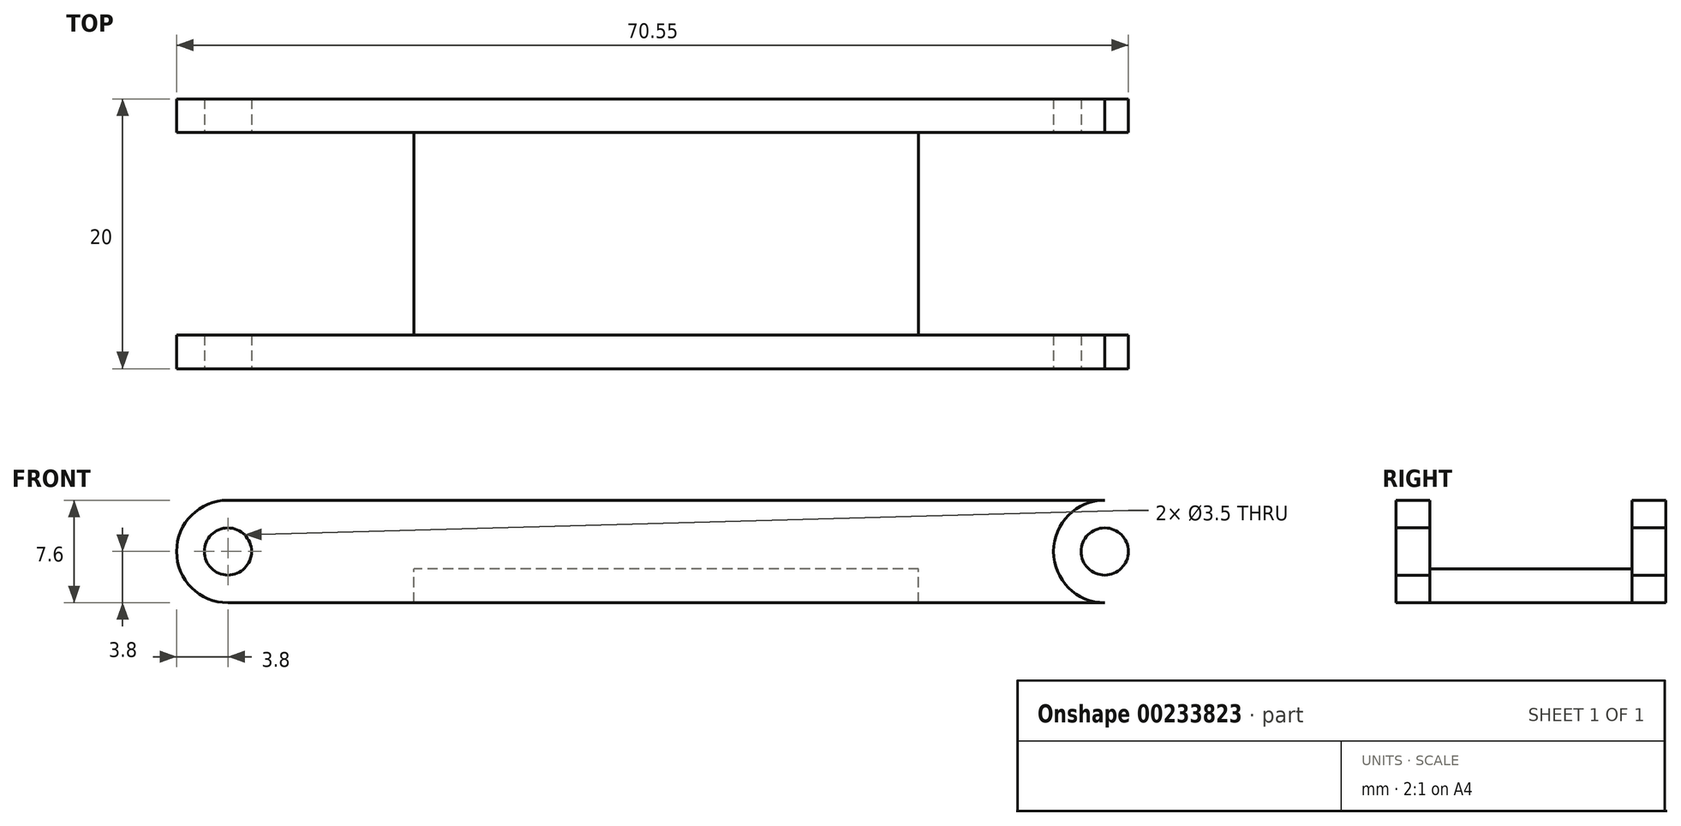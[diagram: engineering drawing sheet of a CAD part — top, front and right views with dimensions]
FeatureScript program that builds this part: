
annotation { "Feature Type Name" : "Feature", "Feature Type Description" : "" }
export const myFeature = defineFeature(function(context is Context, id is Id, definition is map)
    precondition{}
    {
        {
            var Q0;
            Q0=qCreatedBy(makeId("Right.planeOp"),FACE);
            var sketch = newSketch(context, id + "F0", { "sketchPlane" : qUnion([Q0])});
            skLineSegment(sketch, "E0.bottom", {"start": v(-7.5, 0) * mm, "end": v(7.5, 0) * mm});
            skLineSegment(sketch, "E0.top", {"start": v(-7.5, 2.5) * mm, "end": v(7.5, 2.5) * mm});
            skLineSegment(sketch, "E0.left", {"start": v(-7.5, 0) * mm, "end": v(-7.5, 2.5) * mm});
            skLineSegment(sketch, "E0.right", {"start": v(7.5, 0) * mm, "end": v(7.5, 2.5) * mm});
            skLineSegment(sketch, "E1.bottom", {"start": v(-7.5, 0) * mm, "end": v(-10, 0) * mm});
            skLineSegment(sketch, "E1.top", {"start": v(-7.5, 7.6) * mm, "end": v(-10, 7.6) * mm});
            skLineSegment(sketch, "E1.left", {"start": v(-7.5, 0) * mm, "end": v(-7.5, 7.6) * mm});
            skLineSegment(sketch, "E1.right", {"start": v(-10, 0) * mm, "end": v(-10, 7.6) * mm});
            skLineSegment(sketch, "E2.MirrorCS", {"start": v(7.5, 7.6) * mm, "end": v(10, 7.6) * mm});
            skLineSegment(sketch, "E3.MirrorCS", {"start": v(7.5, 0) * mm, "end": v(10, 0) * mm});
            skLineSegment(sketch, "E4.MirrorCS", {"start": v(7.5, 0) * mm, "end": v(7.5, 7.6) * mm});
            skLineSegment(sketch, "E5.MirrorCS", {"start": v(10, 0) * mm, "end": v(10, 7.6) * mm});
            skSolve(sketch);
        }
        {
            var Q0;
            {var subQ0=sQuery(id+"F0.wireOp",EDGE,"E0.bottom");Q0=makeQuery(id+"F0.imprint","IMPRINT",FACE,{"disambiguationData":[TD([[makeQuery(id+"F0.imprint","IMPRINT",EDGE,{"derivedFrom":subQ0}),1.0]])]});}
            extrude(context, id + "F1", {"entities" : qUnion([Q0]), "endBound" : BoundingType.SYMMETRIC, "depth" : 37.4 * mm});
        }
        {
            var Q0;
            {var subQ3=sQuery(id+"F0.wireOp",EDGE,"E1.bottom");Q0=makeQuery(id+"F0.imprint","IMPRINT",FACE,{"disambiguationData":[TD([[makeQuery(id+"F0.imprint","IMPRINT",EDGE,{"derivedFrom":subQ3}),-1.0]])]});}
            var Q1;
            {var subQ2=sQuery(id+"F0.wireOp",EDGE,"E2.MirrorCS");Q1=makeQuery(id+"F0.imprint","IMPRINT",FACE,{"disambiguationData":[TD([[makeQuery(id+"F0.imprint","IMPRINT",EDGE,{"derivedFrom":subQ2}),-1.0]])]});}
            extrude(context, id + "F2", {"entities" : qUnion([Q0, Q1]), "operationType" : NewBodyOperationType.ADD, "endBound" : BoundingType.SYMMETRIC, "depth" : 72.6 * mm});
        }
        {
            var Q0;
            Q0=makeQuery(id+"F2.opExtrude","SWEPT_FACE",FACE,{"disambiguationData":[OSD([sQuery(id+"F0.wireOp",EDGE,"E1.right")])]});
            var sketch = newSketch(context, id + "F3", { "sketchPlane" : qUnion([Q0])});
            skCircle(sketch, "E6", {"center": v(-32.5, 3.8) * mm, "radius": 3.8 * mm});
            skCircle(sketch, "E7", {"center": v(-32.5, 3.8) * mm, "radius": 1.75 * mm});
            skLineSegment(sketch, "E8.0", {"start": v(-32.5, 7.6) * mm, "end": v(-36.3, 7.6) * mm});
            skLineSegment(sketch, "E9.0", {"start": v(-32.5, 0) * mm, "end": v(-36.3, 0) * mm});
            skLineSegment(sketch, "E10", {"start": v(-36.3, 7.6) * mm, "end": v(-40.48, 7.6) * mm});
            skLineSegment(sketch, "E11", {"start": v(-40.48, 7.6) * mm, "end": v(-40.48, 0) * mm});
            skLineSegment(sketch, "E12", {"start": v(-40.48, 0) * mm, "end": v(-36.3, 0) * mm});
            skPoint(sketch, "E13.orphan", {"position": v(36.3, 7.6) * mm});
            skPoint(sketch, "E14.orphan", {"position": v(36.3, 0) * mm});
            skLineSegment(sketch, "E15.MirrorCS", {"start": v(36.3, 7.6) * mm, "end": v(40.48, 7.6) * mm});
            skLineSegment(sketch, "E16.MirrorCS", {"start": v(40.48, 7.6) * mm, "end": v(40.48, 0) * mm});
            skLineSegment(sketch, "E17.MirrorCS", {"start": v(32.5, 0) * mm, "end": v(36.3, 0) * mm});
            skLineSegment(sketch, "E18.MirrorCS", {"start": v(40.48, 0) * mm, "end": v(36.3, 0) * mm});
            skLineSegment(sketch, "E19.MirrorCS", {"start": v(32.5, 7.6) * mm, "end": v(36.3, 7.6) * mm});
            skCircle(sketch, "E20.MirrorC", {"center": v(32.5, 3.8) * mm, "radius": 1.75 * mm});
            skCircle(sketch, "E21.MirrorC", {"center": v(32.5, 3.8) * mm, "radius": 3.8 * mm});
            skSolve(sketch);
        }
        {
            var Q0;
            Q0=makeQuery(id+"F3.imprint","IMPRINT",FACE,{"disambiguationData":[TD([[makeQuery(id+"F3.imprint","IMPRINT",EDGE,{"derivedFrom":sQuery(id+"F3.wireOp",EDGE,"E7")}),1.0]])]});
            var Q1;
            Q1=makeQuery(id+"F3.imprint","IMPRINT",FACE,{"disambiguationData":[TD([[makeQuery(id+"F3.imprint","IMPRINT",EDGE,{"derivedFrom":sQuery(id+"F3.wireOp",EDGE,"E20.MirrorC")}),-1.0]])]});
            var Q2;
            {var subQ3=sQuery(id+"F3.wireOp",EDGE,"E10");Q2=makeQuery(id+"F3.imprint","IMPRINT",FACE,{"disambiguationData":[TD([[makeQuery(id+"F3.imprint","IMPRINT",EDGE,{"derivedFrom":subQ3}),1.0]])]});}
            var Q3;
            {var subQ0=sQuery(id+"F3.wireOp",EDGE,"E9.0");Q3=makeQuery(id+"F3.imprint","IMPRINT",FACE,{"disambiguationData":[TD([[makeQuery(id+"F3.imprint","IMPRINT",EDGE,{"derivedFrom":subQ0}),-1.0]])]});}
            var Q4;
            {var subQ0=sQuery(id+"F3.wireOp",EDGE,"E8.0");Q4=makeQuery(id+"F3.imprint","IMPRINT",FACE,{"disambiguationData":[TD([[makeQuery(id+"F3.imprint","IMPRINT",EDGE,{"derivedFrom":subQ0}),1.0]])]});}
            var Q5;
            {var subQ0=sQuery(id+"F3.wireOp",EDGE,"E19.MirrorCS");Q5=makeQuery(id+"F3.imprint","IMPRINT",FACE,{"disambiguationData":[TD([[makeQuery(id+"F3.imprint","IMPRINT",EDGE,{"derivedFrom":subQ0}),1.0]])]});}
            var Q6;
            {var subQ0=sQuery(id+"F3.wireOp",EDGE,"E17.MirrorCS");Q6=makeQuery(id+"F3.imprint","IMPRINT",FACE,{"disambiguationData":[TD([[makeQuery(id+"F3.imprint","IMPRINT",EDGE,{"derivedFrom":subQ0}),-1.0]])]});}
            var Q7;
            {var subQ3=sQuery(id+"F3.wireOp",EDGE,"E15.MirrorCS");Q7=makeQuery(id+"F3.imprint","IMPRINT",FACE,{"disambiguationData":[TD([[makeQuery(id+"F3.imprint","IMPRINT",EDGE,{"derivedFrom":subQ3}),-1.0]])]});}
            extrude(context, id + "F4", {"entities" : qUnion([Q0, Q1, Q2, Q3, Q4, Q5, Q6, Q7]), "operationType" : NewBodyOperationType.REMOVE, "endBound" : BoundingType.THROUGH_ALL, "oppositeDirection" : true, "depth" : 25 * mm});
        }
    });
